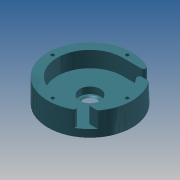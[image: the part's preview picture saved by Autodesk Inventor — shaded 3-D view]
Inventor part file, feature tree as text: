
AUTODESK INVENTOR PART (.ipt)
format: ipt  version: 2013 (Build 170138000, 138)  size: 188,928 bytes
history: native  units: mm
features: extrude x10, sketch x10, fillet x2, pattern_circular x1
ambient origin geometry x8: Origin, YZ Plane, XZ Plane, XY Plane, X Axis, Y Axis, Z Axis, Center Point
bodies: Solid1 (feature_tree)
feature tree (23):
  extrude  "Extrusion1"  Depth=70.0mm
  extrude  "Extrusion2"  Depth=8.0mm TaperAngle=0.0deg
  extrude  "Extrusion3"  Depth=10.0mm TaperAngle=0.0deg
  extrude  "Extrusion4"  Depth=7.0mm TaperAngle=0.0deg
  extrude  "Extrusion5"  Depth=7.5mm
  fillet  "Fillet1"  Radius=7.0mm
  extrude  "Extrusion6"  Depth=40.0mm
  extrude  "Extrusion7"  Depth=7.0mm TaperAngle=0.0deg
  pattern_circular  "Circular Pattern1"  Count=4 Angle=360.0deg
  extrude  "Extrusion8"  Depth=3.5mm
  extrude  "Extrusion9"  Depth=3.0mm TaperAngle=0.0deg
  extrude  "Extrusion10"  Depth=5.5mm
  fillet  "Fillet2"  Radius=4.0mm
  sketch  "Sketch1"  dims[d0=90.0mm d2=70.0mm]
  sketch  "Sketch2"  dims[d3=25.0mm d4=0.0mm d5=8.0mm d6=0.0mm]
  sketch  "Sketch3"  dims[d7=15.0mm d9=10.0mm d10=0.0mm]
  sketch  "Sketch4"  dims[d11=22.0mm d13=7.0mm d14=0.0mm]
  sketch  "Sketch5"  dims[d15=65.0mm d17=7.5mm d18=7.0mm d19=0.0mm]
  sketch  "Sketch6"  dims[d20=2.5mm d21=40.0mm]
  sketch  "Sketch7"  dims[d22=3.5mm d23=7.0mm d24=0.0mm]
  sketch  "Sketch8"  dims[d25=6.0mm]
  sketch  "Sketch9"  dims[d27=3.0mm d28=0.0mm d29=40.0mm d30=360.0deg]
  sketch  "Sketch10"  dims[d32=20.0mm d34=3.5mm d35=3.0mm d36=0.0mm d37=5.5mm d38=4.0mm d39=0.0mm d40=10.0mm d41=0.0mm d42=3.5mm]
